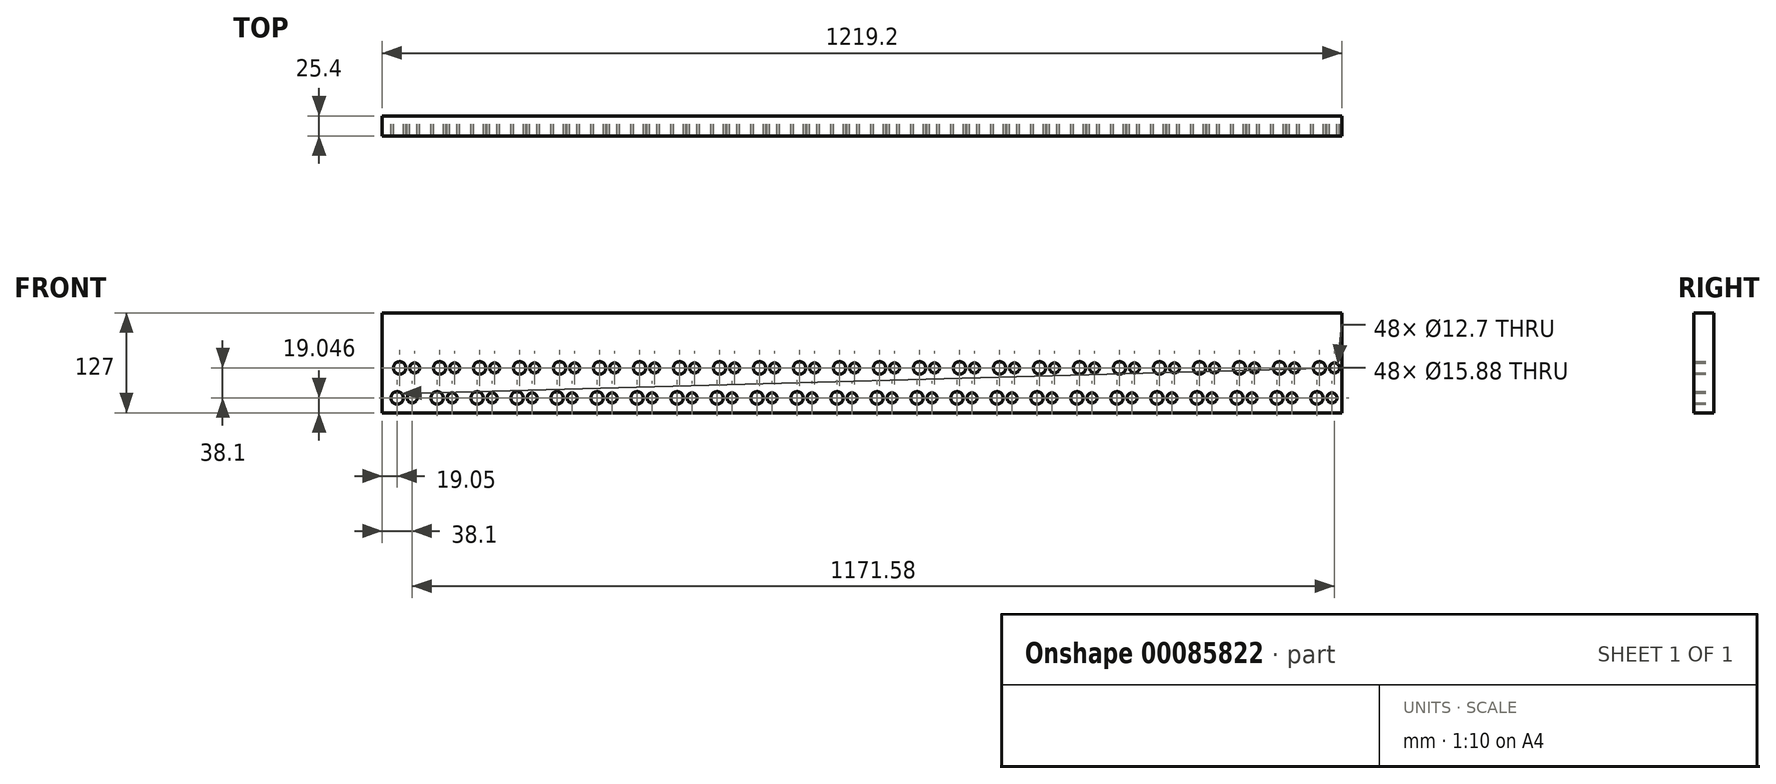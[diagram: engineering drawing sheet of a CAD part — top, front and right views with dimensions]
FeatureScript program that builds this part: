
annotation { "Feature Type Name" : "Feature", "Feature Type Description" : "" }
export const myFeature = defineFeature(function(context is Context, id is Id, definition is map)
    precondition{}
    {
        {
            var Q0;
            Q0=qCreatedBy(makeId("Front.planeOp"),FACE);
            var sketch = newSketch(context, id + "F0", { "sketchPlane" : qUnion([Q0])});
            skLineSegment(sketch, "E0.bottom", {"start": v(0, 309.84) * mm, "end": v(1219.2, 309.84) * mm});
            skLineSegment(sketch, "E0.top", {"start": v(0, 182.84) * mm, "end": v(1219.2, 182.84) * mm});
            skLineSegment(sketch, "E0.left", {"start": v(0, 309.84) * mm, "end": v(0, 182.84) * mm});
            skLineSegment(sketch, "E0.right", {"start": v(1219.2, 309.84) * mm, "end": v(1219.2, 182.84) * mm});
            skLineSegment(sketch, "E1.0", {"start": v(19.05, 201.89) * mm, "end": v(1200.15, 201.89) * mm});
            skCircle(sketch, "E2", {"center": v(19.05, 201.89) * mm, "radius": 7.94 * mm});
            skCircle(sketch, "E3", {"center": v(38.1, 201.89) * mm, "radius": 6.35 * mm});
            skLineSegment(sketch, "E4.direction1", {"start": v(19.05, 201.89) * mm, "end": v(69.85, 201.89) * mm, "construction": true});
            skLineSegment(sketch, "E5.0", {"start": v(19.05, 220.94) * mm, "end": v(1200.15, 220.94) * mm});
            skLineSegment(sketch, "E6.MirrorCS", {"start": v(19.05, 239.99) * mm, "end": v(1200.15, 239.99) * mm});
            skCircle(sketch, "E7.MirrorC", {"center": v(41.28, 239.99) * mm, "radius": 6.35 * mm});
            skCircle(sketch, "E8.MirrorC", {"center": v(22.23, 239.99) * mm, "radius": 7.94 * mm});
            skCircle(sketch, "E9.1.0.0", {"center": v(92.08, 239.99) * mm, "radius": 6.35 * mm});
            skCircle(sketch, "E9.1.0.1", {"center": v(73.03, 239.99) * mm, "radius": 7.94 * mm});
            skCircle(sketch, "E9.2.0.0", {"center": v(142.88, 239.99) * mm, "radius": 6.35 * mm});
            skCircle(sketch, "E9.2.0.1", {"center": v(123.83, 239.99) * mm, "radius": 7.94 * mm});
            skCircle(sketch, "E9.3.0.0", {"center": v(193.68, 239.99) * mm, "radius": 6.35 * mm});
            skCircle(sketch, "E9.3.0.1", {"center": v(174.63, 239.99) * mm, "radius": 7.94 * mm});
            skCircle(sketch, "E9.4.0.0", {"center": v(244.48, 239.99) * mm, "radius": 6.35 * mm});
            skCircle(sketch, "E9.4.0.1", {"center": v(225.43, 239.99) * mm, "radius": 7.94 * mm});
            skCircle(sketch, "E9.5.0.0", {"center": v(295.28, 239.99) * mm, "radius": 6.35 * mm});
            skCircle(sketch, "E9.5.0.1", {"center": v(276.23, 239.99) * mm, "radius": 7.94 * mm});
            skCircle(sketch, "E9.6.0.0", {"center": v(346.08, 239.99) * mm, "radius": 6.35 * mm});
            skCircle(sketch, "E9.6.0.1", {"center": v(327.03, 239.99) * mm, "radius": 7.94 * mm});
            skCircle(sketch, "E9.7.0.0", {"center": v(396.88, 239.99) * mm, "radius": 6.35 * mm});
            skCircle(sketch, "E9.7.0.1", {"center": v(377.83, 239.99) * mm, "radius": 7.94 * mm});
            skCircle(sketch, "E9.8.0.0", {"center": v(447.68, 239.99) * mm, "radius": 6.35 * mm});
            skCircle(sketch, "E9.8.0.1", {"center": v(428.63, 239.99) * mm, "radius": 7.94 * mm});
            skCircle(sketch, "E9.9.0.0", {"center": v(498.48, 239.99) * mm, "radius": 6.35 * mm});
            skCircle(sketch, "E9.9.0.1", {"center": v(479.43, 239.99) * mm, "radius": 7.94 * mm});
            skCircle(sketch, "E9.10.0.0", {"center": v(549.28, 239.99) * mm, "radius": 6.35 * mm});
            skCircle(sketch, "E9.10.0.1", {"center": v(530.23, 239.99) * mm, "radius": 7.94 * mm});
            skCircle(sketch, "E9.11.0.0", {"center": v(600.08, 239.99) * mm, "radius": 6.35 * mm});
            skCircle(sketch, "E9.11.0.1", {"center": v(581.03, 239.99) * mm, "radius": 7.94 * mm});
            skCircle(sketch, "E9.12.0.0", {"center": v(650.88, 239.99) * mm, "radius": 6.35 * mm});
            skCircle(sketch, "E9.12.0.1", {"center": v(631.83, 239.99) * mm, "radius": 7.94 * mm});
            skCircle(sketch, "E9.13.0.0", {"center": v(701.68, 239.99) * mm, "radius": 6.35 * mm});
            skCircle(sketch, "E9.13.0.1", {"center": v(682.63, 239.99) * mm, "radius": 7.94 * mm});
            skCircle(sketch, "E9.14.0.0", {"center": v(752.48, 239.99) * mm, "radius": 6.35 * mm});
            skCircle(sketch, "E9.14.0.1", {"center": v(733.43, 239.99) * mm, "radius": 7.94 * mm});
            skCircle(sketch, "E9.15.0.0", {"center": v(803.28, 239.99) * mm, "radius": 6.35 * mm});
            skCircle(sketch, "E9.15.0.1", {"center": v(784.23, 239.99) * mm, "radius": 7.94 * mm});
            skCircle(sketch, "E9.16.0.0", {"center": v(854.08, 239.99) * mm, "radius": 6.35 * mm});
            skCircle(sketch, "E9.16.0.1", {"center": v(835.03, 239.99) * mm, "radius": 7.94 * mm});
            skCircle(sketch, "E9.17.0.0", {"center": v(904.88, 239.99) * mm, "radius": 6.35 * mm});
            skCircle(sketch, "E9.17.0.1", {"center": v(885.83, 239.99) * mm, "radius": 7.94 * mm});
            skCircle(sketch, "E9.18.0.0", {"center": v(955.68, 239.99) * mm, "radius": 6.35 * mm});
            skCircle(sketch, "E9.18.0.1", {"center": v(936.63, 239.99) * mm, "radius": 7.94 * mm});
            skCircle(sketch, "E9.19.0.0", {"center": v(1006.48, 239.99) * mm, "radius": 6.35 * mm});
            skCircle(sketch, "E9.19.0.1", {"center": v(987.43, 239.99) * mm, "radius": 7.94 * mm});
            skCircle(sketch, "E9.20.0.0", {"center": v(1057.28, 239.99) * mm, "radius": 6.35 * mm});
            skCircle(sketch, "E9.20.0.1", {"center": v(1038.23, 239.99) * mm, "radius": 7.94 * mm});
            skCircle(sketch, "E9.21.0.0", {"center": v(1108.08, 239.99) * mm, "radius": 6.35 * mm});
            skCircle(sketch, "E9.21.0.1", {"center": v(1089.03, 239.99) * mm, "radius": 7.94 * mm});
            skCircle(sketch, "E9.22.0.0", {"center": v(1158.88, 239.99) * mm, "radius": 6.35 * mm});
            skCircle(sketch, "E9.22.0.1", {"center": v(1139.83, 239.99) * mm, "radius": 7.94 * mm});
            skCircle(sketch, "E9.23.0.0", {"center": v(1209.68, 239.99) * mm, "radius": 6.35 * mm});
            skCircle(sketch, "E9.23.0.1", {"center": v(1190.63, 239.99) * mm, "radius": 7.94 * mm});
            skCircle(sketch, "E9.24.0.0", {"center": v(1260.48, 239.99) * mm, "radius": 6.35 * mm});
            skCircle(sketch, "E9.24.0.1", {"center": v(1241.43, 239.99) * mm, "radius": 7.94 * mm});
            skLineSegment(sketch, "E9.direction1", {"start": v(41.28, 239.99) * mm, "end": v(92.08, 239.99) * mm, "construction": true});
            skCircle(sketch, "E10.1.0.0", {"center": v(69.85, 201.89) * mm, "radius": 7.94 * mm});
            skCircle(sketch, "E10.1.0.1", {"center": v(88.9, 201.89) * mm, "radius": 6.35 * mm});
            skCircle(sketch, "E10.2.0.0", {"center": v(120.65, 201.89) * mm, "radius": 7.94 * mm});
            skCircle(sketch, "E10.2.0.1", {"center": v(139.7, 201.89) * mm, "radius": 6.35 * mm});
            skCircle(sketch, "E10.3.0.0", {"center": v(171.45, 201.89) * mm, "radius": 7.94 * mm});
            skCircle(sketch, "E10.3.0.1", {"center": v(190.5, 201.89) * mm, "radius": 6.35 * mm});
            skCircle(sketch, "E10.4.0.0", {"center": v(222.25, 201.89) * mm, "radius": 7.94 * mm});
            skCircle(sketch, "E10.4.0.1", {"center": v(241.3, 201.89) * mm, "radius": 6.35 * mm});
            skCircle(sketch, "E10.5.0.0", {"center": v(273.05, 201.89) * mm, "radius": 7.94 * mm});
            skCircle(sketch, "E10.5.0.1", {"center": v(292.1, 201.89) * mm, "radius": 6.35 * mm});
            skCircle(sketch, "E10.6.0.0", {"center": v(323.85, 201.89) * mm, "radius": 7.94 * mm});
            skCircle(sketch, "E10.6.0.1", {"center": v(342.9, 201.89) * mm, "radius": 6.35 * mm});
            skCircle(sketch, "E10.7.0.0", {"center": v(374.65, 201.89) * mm, "radius": 7.94 * mm});
            skCircle(sketch, "E10.7.0.1", {"center": v(393.7, 201.89) * mm, "radius": 6.35 * mm});
            skCircle(sketch, "E10.8.0.0", {"center": v(425.45, 201.89) * mm, "radius": 7.94 * mm});
            skCircle(sketch, "E10.8.0.1", {"center": v(444.5, 201.89) * mm, "radius": 6.35 * mm});
            skCircle(sketch, "E10.9.0.0", {"center": v(476.25, 201.89) * mm, "radius": 7.94 * mm});
            skCircle(sketch, "E10.9.0.1", {"center": v(495.3, 201.89) * mm, "radius": 6.35 * mm});
            skCircle(sketch, "E10.10.0.0", {"center": v(527.05, 201.89) * mm, "radius": 7.94 * mm});
            skCircle(sketch, "E10.10.0.1", {"center": v(546.1, 201.89) * mm, "radius": 6.35 * mm});
            skCircle(sketch, "E10.11.0.0", {"center": v(577.85, 201.89) * mm, "radius": 7.94 * mm});
            skCircle(sketch, "E10.11.0.1", {"center": v(596.9, 201.89) * mm, "radius": 6.35 * mm});
            skCircle(sketch, "E10.12.0.0", {"center": v(628.65, 201.89) * mm, "radius": 7.94 * mm});
            skCircle(sketch, "E10.12.0.1", {"center": v(647.7, 201.89) * mm, "radius": 6.35 * mm});
            skCircle(sketch, "E10.13.0.0", {"center": v(679.45, 201.89) * mm, "radius": 7.94 * mm});
            skCircle(sketch, "E10.13.0.1", {"center": v(698.5, 201.89) * mm, "radius": 6.35 * mm});
            skCircle(sketch, "E10.14.0.0", {"center": v(730.25, 201.89) * mm, "radius": 7.94 * mm});
            skCircle(sketch, "E10.14.0.1", {"center": v(749.3, 201.89) * mm, "radius": 6.35 * mm});
            skCircle(sketch, "E10.15.0.0", {"center": v(781.05, 201.89) * mm, "radius": 7.94 * mm});
            skCircle(sketch, "E10.15.0.1", {"center": v(800.1, 201.89) * mm, "radius": 6.35 * mm});
            skCircle(sketch, "E10.16.0.0", {"center": v(831.85, 201.89) * mm, "radius": 7.94 * mm});
            skCircle(sketch, "E10.16.0.1", {"center": v(850.9, 201.89) * mm, "radius": 6.35 * mm});
            skCircle(sketch, "E10.17.0.0", {"center": v(882.65, 201.89) * mm, "radius": 7.94 * mm});
            skCircle(sketch, "E10.17.0.1", {"center": v(901.7, 201.89) * mm, "radius": 6.35 * mm});
            skCircle(sketch, "E10.18.0.0", {"center": v(933.45, 201.89) * mm, "radius": 7.94 * mm});
            skCircle(sketch, "E10.18.0.1", {"center": v(952.5, 201.89) * mm, "radius": 6.35 * mm});
            skCircle(sketch, "E10.19.0.0", {"center": v(984.25, 201.89) * mm, "radius": 7.94 * mm});
            skCircle(sketch, "E10.19.0.1", {"center": v(1003.3, 201.89) * mm, "radius": 6.35 * mm});
            skCircle(sketch, "E10.20.0.0", {"center": v(1035.05, 201.89) * mm, "radius": 7.94 * mm});
            skCircle(sketch, "E10.20.0.1", {"center": v(1054.1, 201.89) * mm, "radius": 6.35 * mm});
            skCircle(sketch, "E10.21.0.0", {"center": v(1085.85, 201.89) * mm, "radius": 7.94 * mm});
            skCircle(sketch, "E10.21.0.1", {"center": v(1104.9, 201.89) * mm, "radius": 6.35 * mm});
            skCircle(sketch, "E10.22.0.0", {"center": v(1136.65, 201.89) * mm, "radius": 7.94 * mm});
            skCircle(sketch, "E10.22.0.1", {"center": v(1155.7, 201.89) * mm, "radius": 6.35 * mm});
            skCircle(sketch, "E10.23.0.0", {"center": v(1187.45, 201.89) * mm, "radius": 7.94 * mm});
            skCircle(sketch, "E10.23.0.1", {"center": v(1206.5, 201.89) * mm, "radius": 6.35 * mm});
            skCircle(sketch, "E10.24.0.0", {"center": v(1238.25, 201.89) * mm, "radius": 7.94 * mm});
            skCircle(sketch, "E10.24.0.1", {"center": v(1257.3, 201.89) * mm, "radius": 6.35 * mm});
            skSolve(sketch);
        }
        {
            var Q0;
            Q0=makeQuery(id+"F0.imprint","IMPRINT",FACE,{"disambiguationData":[TD([[makeQuery(id+"F0.imprint","IMPRINT",EDGE,{"derivedFrom":sQuery(id+"F0.wireOp",EDGE,"E0.bottom")}),-1.0]])]});
            extrude(context, id + "F1", {"entities" : qUnion([Q0]), "depth" : 25.4 * mm, "offsetDistance" : 25.4 * mm});
        }
    });
